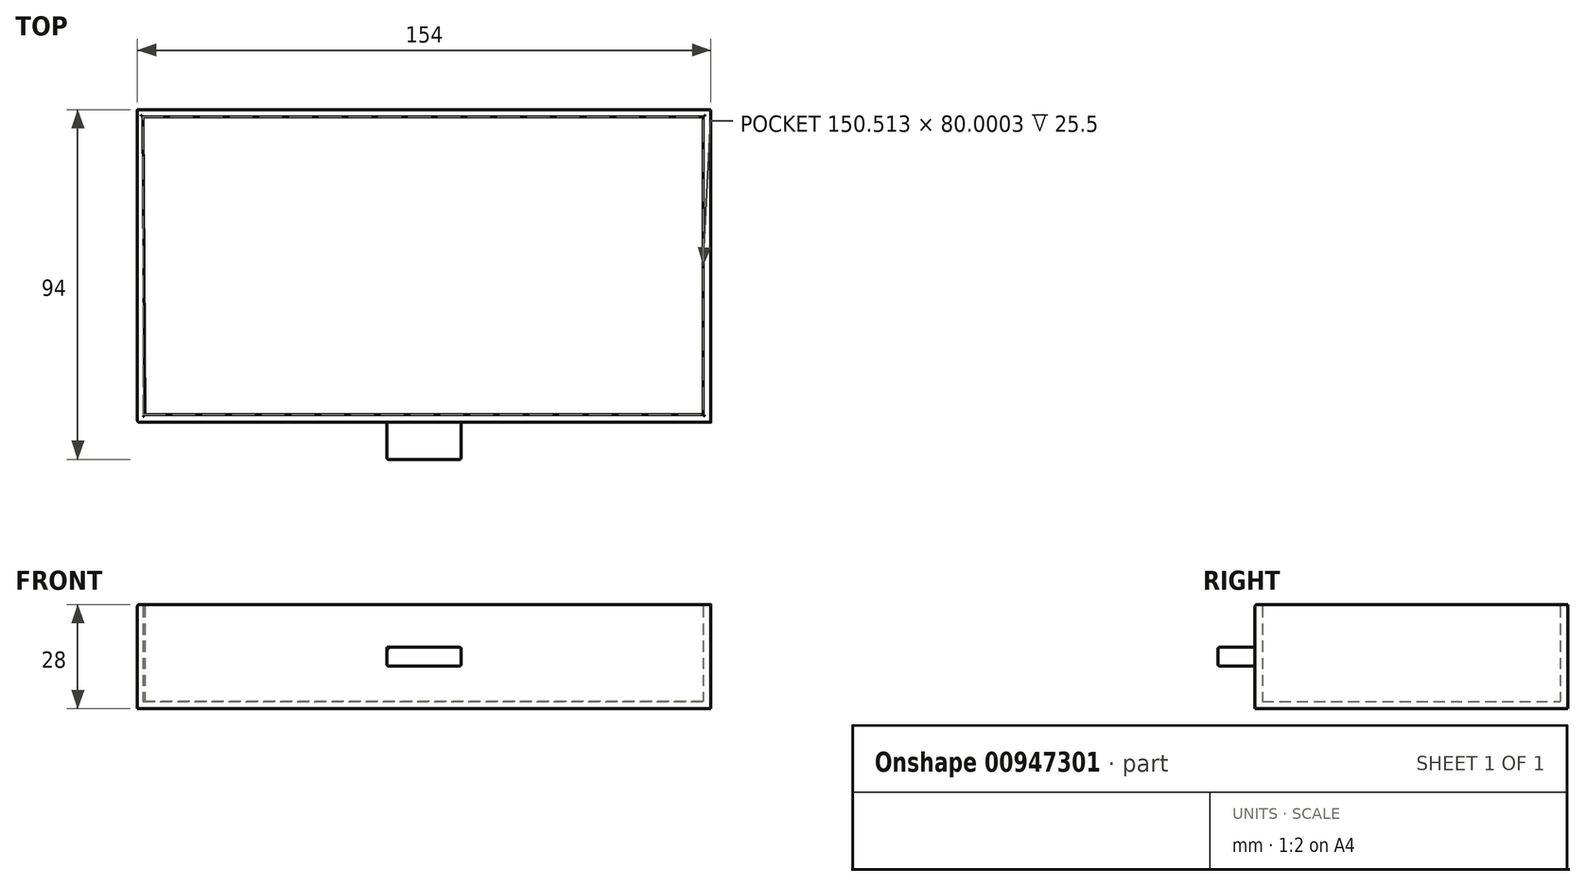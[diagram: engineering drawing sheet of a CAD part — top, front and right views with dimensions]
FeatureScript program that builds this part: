
annotation { "Feature Type Name" : "Feature", "Feature Type Description" : "" }
export const myFeature = defineFeature(function(context is Context, id is Id, definition is map)
    precondition{}
    {
        {
            var Q0;
            Q0=qCreatedBy(makeId("Top.planeOp"),FACE);
            var sketch = newSketch(context, id + "F0", { "sketchPlane" : qUnion([Q0])});
            skLineSegment(sketch, "E0", {"start": v(-84.28, -100) * mm, "end": v(85.72, -100) * mm});
            skLineSegment(sketch, "E1", {"start": v(-84.28, -100) * mm, "end": v(-84.28, 0) * mm});
            skLineSegment(sketch, "E2", {"start": v(85.72, -100) * mm, "end": v(85.72, 0) * mm});
            skLineSegment(sketch, "E3", {"start": v(85.72, 0) * mm, "end": v(-84.28, 0) * mm});
            skSolve(sketch);
        }
        {
            var Q0;
            Q0=makeQuery(id+"F0.imprint","IMPRINT",FACE,{"disambiguationData":[TD([[makeQuery(id+"F0.imprint","IMPRINT",EDGE,{"derivedFrom":sQuery(id+"F0.wireOp",EDGE,"E0")}),1.0]])]});
            extrude(context, id + "F1", {"entities" : qUnion([Q0]), "depth" : 2 * mm, "offsetDistance" : 25 * mm});
        }
        {
            var Q0;
            Q0=makeQuery(id+"F1.opExtrude","CAP_FACE",FACE,{"disambiguationData":[OSD([sQuery(id+"F0.wireOp",EDGE,"E0"),sQuery(id+"F0.wireOp",EDGE,"E1"),sQuery(id+"F0.wireOp",EDGE,"E2"),sQuery(id+"F0.wireOp",EDGE,"E3")])],"isStart":false});
            var sketch = newSketch(context, id + "F2", { "sketchPlane" : qUnion([Q0])});
            skLineSegment(sketch, "E4", {"start": v(83.72, -98) * mm, "end": v(-82.28, -98) * mm});
            skLineSegment(sketch, "E5", {"start": v(83.72, -2) * mm, "end": v(83.72, -98) * mm});
            skLineSegment(sketch, "E6", {"start": v(83.72, -2) * mm, "end": v(-82.9, -2) * mm});
            skLineSegment(sketch, "E7", {"start": v(-82.28, -98) * mm, "end": v(-82.9, -2) * mm});
            skSolve(sketch);
        }
        {
            var Q0;
            Q0=makeQuery(id+"F2.imprint","IMPRINT",FACE,{"disambiguationData":[TD([[makeQuery(id+"F2.imprint","IMPRINT",EDGE,{"derivedFrom":sQuery(id+"F2.wireOp",EDGE,"E4")}),1.0]])]});
            extrude(context, id + "F3", {"entities" : qUnion([Q0]), "operationType" : NewBodyOperationType.ADD, "depth" : 26 * mm, "offsetDistance" : 25 * mm});
        }
        {
            var Q0;
            Q0=makeQuery(id+"F1.opExtrude","CAP_FACE",FACE,{"disambiguationData":[OSD([sQuery(id+"F0.wireOp",EDGE,"E0"),sQuery(id+"F0.wireOp",EDGE,"E1"),sQuery(id+"F0.wireOp",EDGE,"E2"),sQuery(id+"F0.wireOp",EDGE,"E3")])],"isStart":false});
            var sketch = newSketch(context, id + "F4", { "sketchPlane" : qUnion([Q0])});
            skLineSegment(sketch, "E8", {"start": v(83.72, -98) * mm, "end": v(67.72, -98) * mm});
            skLineSegment(sketch, "E9", {"start": v(67.72, -98) * mm, "end": v(67.72, -2) * mm});
            skLineSegment(sketch, "E10", {"start": v(67.72, -2) * mm, "end": v(69.72, -2) * mm});
            skLineSegment(sketch, "E11", {"start": v(69.72, -2) * mm, "end": v(69.72, -98) * mm});
            skLineSegment(sketch, "E12", {"start": v(69.72, -98) * mm, "end": v(67.72, -98) * mm});
            skSolve(sketch);
        }
        {
            var Q0;
            {var subQ0=sQuery(id+"F4.wireOp",EDGE,"E9");Q0=makeQuery(id+"F4.imprint","IMPRINT",FACE,{"disambiguationData":[TD([[makeQuery(id+"F4.imprint","IMPRINT",EDGE,{"derivedFrom":subQ0}),-1.0]])]});}
            extrude(context, id + "F5", {"entities" : qUnion([Q0]), "operationType" : NewBodyOperationType.ADD, "depth" : 26 * mm, "offsetDistance" : 25 * mm});
        }
        {
            var Q0;
            Q0=makeQuery(id+"F5.boolean.opBoolean","MERGE",FACE,{"derivedFrom":[makeQuery(id+"F3.opExtrude","CAP_FACE",FACE,{"disambiguationData":[OSD([sQuery(id+"F0.wireOp",EDGE,"E0"),sQuery(id+"F0.wireOp",EDGE,"E1"),sQuery(id+"F0.wireOp",EDGE,"E2"),sQuery(id+"F0.wireOp",EDGE,"E3"),sQuery(id+"F2.wireOp",EDGE,"E4"),sQuery(id+"F2.wireOp",EDGE,"E5"),sQuery(id+"F2.wireOp",EDGE,"E6"),sQuery(id+"F2.wireOp",EDGE,"E7")])],"isStart":false}),makeQuery(id+"F5.opExtrude","CAP_FACE",FACE,{"disambiguationData":[OSD([sQuery(id+"F4.wireOp",EDGE,"E8"),sQuery(id+"F4.wireOp",EDGE,"E9"),sQuery(id+"F4.wireOp",EDGE,"E10"),sQuery(id+"F4.wireOp",EDGE,"E11")])],"isStart":false})]});
            var sketch = newSketch(context, id + "F6", { "sketchPlane" : qUnion([Q0])});
            skLineSegment(sketch, "E13", {"start": v(69.72, -98) * mm, "end": v(69.72, -100) * mm});
            skLineSegment(sketch, "E14", {"start": v(69.72, -100) * mm, "end": v(85.72, -100) * mm});
            skLineSegment(sketch, "E15", {"start": v(85.72, -100) * mm, "end": v(85.72, 0) * mm});
            skLineSegment(sketch, "E16", {"start": v(85.72, 0) * mm, "end": v(69.72, 0) * mm});
            skLineSegment(sketch, "E17", {"start": v(69.72, 0) * mm, "end": v(69.72, -100) * mm});
            skSolve(sketch);
        }
        {
            var Q0;
            {var subQ4=sQuery(id+"F2.wireOp",EDGE,"E5");Q0=makeQuery(id+"F6.imprint","IMPRINT",FACE,{"disambiguationData":[TD([[makeQuery(id+"F6.imprint","IMPRINT",EDGE,{"derivedFrom":makeQuery(id+"F3.opExtrude","CAP_EDGE",EDGE,{"disambiguationData":[OSD([subQ4])],"isStart":false})}),-1.0]])]});}
            var Q1;
            Q1=makeQuery(id+"F6.imprint","IMPRINT",FACE,{"disambiguationData":[TD([[makeQuery(id+"F6.imprint","IMPRINT",EDGE,{"derivedFrom":sQuery(id+"F6.wireOp",EDGE,"E13")}),1.0]])]});
            extrude(context, id + "F7", {"entities" : qUnion([Q0, Q1]), "operationType" : NewBodyOperationType.REMOVE, "oppositeDirection" : true, "depth" : 30 * mm, "offsetDistance" : 25 * mm});
        }
        {
            var Q0;
            {var subQ0=sQuery(id+"F0.wireOp",EDGE,"E0");Q0=makeQuery(id+"F3.boolean.opBoolean","MERGE",FACE,{"derivedFrom":[makeQuery(id+"F1.opExtrude","SWEPT_FACE",FACE,{"disambiguationData":[OSD([subQ0])]}),makeQuery(id+"F3.opExtrude","SWEPT_FACE",FACE,{"disambiguationData":[OSD([subQ0])]})]});}
            var sketch = newSketch(context, id + "F8", { "sketchPlane" : qUnion([Q0])});
            skLineSegment(sketch, "E18", {"start": v(-84.28, 14) * mm, "end": v(69.72, 14) * mm});
            skLineSegment(sketch, "E19", {"start": v(-7.28, 28) * mm, "end": v(-7.28, 0) * mm});
            skLineSegment(sketch, "E20", {"start": v(-7.28, 14) * mm, "end": v(2.72, 14) * mm});
            skLineSegment(sketch, "E21", {"start": v(2.72, 14) * mm, "end": v(2.72, 16.5) * mm});
            skLineSegment(sketch, "E22", {"start": v(2.72, 16.5) * mm, "end": v(-17.28, 16.5) * mm});
            skLineSegment(sketch, "E23", {"start": v(-17.28, 16.5) * mm, "end": v(-17.28, 11.5) * mm});
            skLineSegment(sketch, "E24", {"start": v(-17.28, 11.5) * mm, "end": v(2.72, 11.5) * mm});
            skLineSegment(sketch, "E25", {"start": v(2.72, 11.5) * mm, "end": v(2.72, 14) * mm});
            skSolve(sketch);
        }
        {
            var Q0;
            {var subQ0=sQuery(id+"F8.wireOp",EDGE,"E21");Q0=makeQuery(id+"F8.imprint","IMPRINT",FACE,{"disambiguationData":[TD([[makeQuery(id+"F8.imprint","IMPRINT",EDGE,{"derivedFrom":subQ0}),1.0]])]});}
            var Q1;
            {var subQ0=sQuery(id+"F8.wireOp",EDGE,"E23");var subQ1=sQuery(id+"F8.wireOp",EDGE,"E18");var subQ2=makeQuery(id+"F8.imprint","INTERSECT",VERTEX,{"derivedFrom":[subQ1,subQ0]});Q1=makeQuery(id+"F8.imprint","IMPRINT",FACE,{"disambiguationData":[TD([[makeQuery(id+"F8.imprint","IMPRINT",EDGE,{"disambiguationData":[TD([[subQ2,-1.0]])],"derivedFrom":subQ1}),1.0]])]});}
            var Q2;
            {var subQ0=sQuery(id+"F8.wireOp",EDGE,"E23");var subQ1=sQuery(id+"F8.wireOp",EDGE,"E18");var subQ2=makeQuery(id+"F8.imprint","INTERSECT",VERTEX,{"derivedFrom":[subQ1,subQ0]});Q2=makeQuery(id+"F8.imprint","IMPRINT",FACE,{"disambiguationData":[TD([[makeQuery(id+"F8.imprint","IMPRINT",EDGE,{"disambiguationData":[TD([[subQ2,-1.0]])],"derivedFrom":subQ1}),-1.0]])]});}
            var Q3;
            {var subQ0=sQuery(id+"F8.wireOp",EDGE,"E25");Q3=makeQuery(id+"F8.imprint","IMPRINT",FACE,{"disambiguationData":[TD([[makeQuery(id+"F8.imprint","IMPRINT",EDGE,{"derivedFrom":subQ0}),1.0]])]});}
            extrude(context, id + "F9", {"entities" : qUnion([Q0, Q1, Q2, Q3]), "operationType" : NewBodyOperationType.ADD, "depth" : 10 * mm, "offsetDistance" : 25 * mm});
        }
        {
            var Q0;
            Q0=makeQuery(id+"F5.boolean.opBoolean","SPLIT",FACE,{"disambiguationData":[TD([makeQuery(id+"F3.opExtrude","SWEPT_FACE",FACE,{"disambiguationData":[OSD([sQuery(id+"F2.wireOp",EDGE,"E7")])]})])],"derivedFrom":makeQuery(id+"F1.opExtrude","CAP_FACE",FACE,{"disambiguationData":[OSD([sQuery(id+"F0.wireOp",EDGE,"E0"),sQuery(id+"F0.wireOp",EDGE,"E1"),sQuery(id+"F0.wireOp",EDGE,"E2"),sQuery(id+"F0.wireOp",EDGE,"E3")])],"isStart":false})});
            var sketch = newSketch(context, id + "F10", { "sketchPlane" : qUnion([Q0])});
            skLineSegment(sketch, "E26", {"start": v(-82.9, -2) * mm, "end": v(-82.8, -18) * mm});
            skLineSegment(sketch, "E27", {"start": v(-82.8, -18) * mm, "end": v(67.72, -18) * mm});
            skLineSegment(sketch, "E28", {"start": v(-82.8, -18) * mm, "end": v(-82.8, -16) * mm});
            skLineSegment(sketch, "E29", {"start": v(-82.8, -16) * mm, "end": v(67.72, -16) * mm});
            skLineSegment(sketch, "E30", {"start": v(67.72, -16) * mm, "end": v(67.72, -18) * mm});
            skSolve(sketch);
        }
        {
            var Q0;
            {var subQ0=sQuery(id+"F10.wireOp",EDGE,"E27");Q0=makeQuery(id+"F10.imprint","IMPRINT",FACE,{"disambiguationData":[TD([[makeQuery(id+"F10.imprint","IMPRINT",EDGE,{"derivedFrom":subQ0}),1.0]])]});}
            extrude(context, id + "F11", {"entities" : qUnion([Q0]), "operationType" : NewBodyOperationType.ADD, "depth" : 26 * mm, "offsetDistance" : 25 * mm});
        }
        {
            var Q0;
            Q0=makeQuery(id+"F11.boolean.opBoolean","MERGE",FACE,{"derivedFrom":[makeQuery(id+"F5.boolean.opBoolean","MERGE",FACE,{"derivedFrom":[makeQuery(id+"F3.opExtrude","CAP_FACE",FACE,{"disambiguationData":[OSD([sQuery(id+"F0.wireOp",EDGE,"E0"),sQuery(id+"F0.wireOp",EDGE,"E1"),sQuery(id+"F0.wireOp",EDGE,"E2"),sQuery(id+"F0.wireOp",EDGE,"E3"),sQuery(id+"F2.wireOp",EDGE,"E4"),sQuery(id+"F2.wireOp",EDGE,"E5"),sQuery(id+"F2.wireOp",EDGE,"E6"),sQuery(id+"F2.wireOp",EDGE,"E7")])],"isStart":false}),makeQuery(id+"F5.opExtrude","CAP_FACE",FACE,{"disambiguationData":[OSD([sQuery(id+"F4.wireOp",EDGE,"E8"),sQuery(id+"F4.wireOp",EDGE,"E9"),sQuery(id+"F4.wireOp",EDGE,"E10"),sQuery(id+"F4.wireOp",EDGE,"E11")])],"isStart":false})]}),makeQuery(id+"F11.opExtrude","CAP_FACE",FACE,{"disambiguationData":[OSD([sQuery(id+"F10.wireOp",EDGE,"E26"),sQuery(id+"F10.wireOp",EDGE,"E27"),sQuery(id+"F10.wireOp",EDGE,"E29"),sQuery(id+"F10.wireOp",EDGE,"E30")])],"isStart":false})]});
            var sketch = newSketch(context, id + "F12", { "sketchPlane" : qUnion([Q0])});
            skLineSegment(sketch, "E31", {"start": v(-82.8, -16) * mm, "end": v(69.72, -16) * mm});
            skLineSegment(sketch, "E32", {"start": v(69.72, -16) * mm, "end": v(69.72, 0) * mm});
            skLineSegment(sketch, "E33", {"start": v(69.72, 0) * mm, "end": v(-84.28, 0) * mm});
            skLineSegment(sketch, "E34", {"start": v(-84.28, 0) * mm, "end": v(-84.28, -16) * mm});
            skLineSegment(sketch, "E35", {"start": v(-84.28, -16) * mm, "end": v(-82.8, -16) * mm});
            skSolve(sketch);
        }
        {
            var Q0;
            {var subQ12=sQuery(id+"F12.wireOp",EDGE,"E32");Q0=makeQuery(id+"F12.imprint","IMPRINT",FACE,{"disambiguationData":[TD([[makeQuery(id+"F12.imprint","IMPRINT",EDGE,{"derivedFrom":subQ12}),-1.0]])]});}
            var Q1;
            {var subQ3=sQuery(id+"F2.wireOp",EDGE,"E7");var subQ4=makeQuery(id+"F3.opExtrude","SWEPT_FACE",FACE,{"disambiguationData":[OSD([subQ3])]});var subQ5=sQuery(id+"F2.wireOp",EDGE,"E6");Q1=makeQuery(id+"F12.imprint","IMPRINT",FACE,{"disambiguationData":[TD([[makeQuery(id+"F12.imprint","IMPRINT",EDGE,{"derivedFrom":makeQuery(id+"F5.boolean.opBoolean","SPLIT",EDGE,{"disambiguationData":[TD([subQ4])],"derivedFrom":makeQuery(id+"F3.opExtrude","CAP_EDGE",EDGE,{"disambiguationData":[OSD([subQ5])],"isStart":false})})}),1.0]])]});}
            extrude(context, id + "F13", {"entities" : qUnion([Q0, Q1]), "operationType" : NewBodyOperationType.REMOVE, "oppositeDirection" : true, "depth" : 30 * mm, "offsetDistance" : 25 * mm});
        }
        {
            var Q0;
            {var subQ0=sQuery(id+"F2.wireOp",EDGE,"E7");var subQ1=sQuery(id+"F2.wireOp",EDGE,"E4");Q0=makeQuery(id+"F11.boolean.opBoolean","SPLIT",EDGE,{"disambiguationData":[TD([makeQuery(id+"F3.opExtrude","SWEPT_FACE",FACE,{"disambiguationData":[OSD([subQ1])]})])],"derivedFrom":makeQuery(id+"F3.opExtrude","CAP_EDGE",EDGE,{"disambiguationData":[OSD([subQ0])],"isStart":false})});}
            var Q1;
            Q1=makeQuery(id+"F11.opExtrude","CAP_EDGE",EDGE,{"disambiguationData":[OSD([sQuery(id+"F10.wireOp",EDGE,"E27")])],"isStart":false});
            var Q2;
            Q2=makeQuery(id+"F13.boolean.opBoolean","MERGE",EDGE,{"derivedFrom":[makeQuery(id+"F11.opExtrude","CAP_EDGE",EDGE,{"disambiguationData":[OSD([sQuery(id+"F10.wireOp",EDGE,"E29")])],"isStart":false})],"fromTools":[makeQuery(id+"F13.opExtrude","CAP_EDGE",EDGE,{"disambiguationData":[OSD([sQuery(id+"F12.wireOp",EDGE,"E31"),sQuery(id+"F12.wireOp",EDGE,"E35")])],"isStart":true})]});
            var Q3;
            Q3=makeQuery(id+"F3.opExtrude","CAP_EDGE",EDGE,{"disambiguationData":[OSD([sQuery(id+"F0.wireOp",EDGE,"E1")])],"isStart":false});
            var Q4;
            {var subQ1=sQuery(id+"F2.wireOp",EDGE,"E7");var subQ2=sQuery(id+"F2.wireOp",EDGE,"E4");Q4=makeQuery(id+"F5.boolean.opBoolean","SPLIT",EDGE,{"disambiguationData":[TD([makeQuery(id+"F3.opExtrude","SWEPT_FACE",FACE,{"disambiguationData":[OSD([subQ1])]})])],"derivedFrom":makeQuery(id+"F3.opExtrude","CAP_EDGE",EDGE,{"disambiguationData":[OSD([subQ2])],"isStart":false})});}
            var Q5;
            Q5=makeQuery(id+"F3.opExtrude","CAP_EDGE",EDGE,{"disambiguationData":[OSD([sQuery(id+"F0.wireOp",EDGE,"E0")])],"isStart":false});
            var Q6;
            {var subQ0=sQuery(id+"F4.wireOp",EDGE,"E9");var subQ1=sQuery(id+"F2.wireOp",EDGE,"E4");Q6=makeQuery(id+"F11.boolean.opBoolean","SPLIT",EDGE,{"disambiguationData":[TD([makeQuery(id+"F3.opExtrude","SWEPT_FACE",FACE,{"disambiguationData":[OSD([subQ1])]})])],"derivedFrom":makeQuery(id+"F5.opExtrude","CAP_EDGE",EDGE,{"disambiguationData":[OSD([subQ0])],"isStart":false})});}
            var Q7;
            Q7=makeQuery(id+"F7.boolean.opBoolean","MERGE",EDGE,{"derivedFrom":[makeQuery(id+"F5.opExtrude","CAP_EDGE",EDGE,{"disambiguationData":[OSD([sQuery(id+"F4.wireOp",EDGE,"E11")])],"isStart":false})],"fromTools":[makeQuery(id+"F7.opExtrude","CAP_EDGE",EDGE,{"disambiguationData":[OSD([sQuery(id+"F6.wireOp",EDGE,"E13"),sQuery(id+"F6.wireOp",EDGE,"E17")])],"isStart":true})]});
            var Q8;
            Q8=makeQuery(id+"F13.boolean.opBoolean","COPY",EDGE,{"derivedFrom":makeQuery(id+"F13.opExtrude","SWEPT_EDGE",EDGE,{"disambiguationData":[OSD([sQuery(id+"F4.wireOp",EDGE,"E11"),sQuery(id+"F6.wireOp",EDGE,"E13"),sQuery(id+"F6.wireOp",EDGE,"E17"),sQuery(id+"F12.wireOp",EDGE,"E31"),sQuery(id+"F12.wireOp",EDGE,"E32")])]})});
            var Q9;
            Q9=makeQuery(id+"F7.boolean.opBoolean","COPY",EDGE,{"derivedFrom":makeQuery(id+"F7.opExtrude","SWEPT_EDGE",EDGE,{"disambiguationData":[OSD([sQuery(id+"F0.wireOp",EDGE,"E0"),sQuery(id+"F6.wireOp",EDGE,"E13"),sQuery(id+"F6.wireOp",EDGE,"E14")])]})});
            var Q10;
            Q10=makeQuery(id+"F9.opExtrude","SWEPT_EDGE",EDGE,{"disambiguationData":[OSD([sQuery(id+"F8.wireOp",EDGE,"E21"),sQuery(id+"F8.wireOp",EDGE,"E22")])]});
            var Q11;
            Q11=makeQuery(id+"F9.opExtrude","SWEPT_EDGE",EDGE,{"disambiguationData":[OSD([sQuery(id+"F8.wireOp",EDGE,"E24"),sQuery(id+"F8.wireOp",EDGE,"E25")])]});
            var Q12;
            Q12=makeQuery(id+"F9.opExtrude","CAP_EDGE",EDGE,{"disambiguationData":[OSD([sQuery(id+"F8.wireOp",EDGE,"E21"),sQuery(id+"F8.wireOp",EDGE,"E25")])],"isStart":true});
            var Q13;
            Q13=makeQuery(id+"F9.opExtrude","CAP_EDGE",EDGE,{"disambiguationData":[OSD([sQuery(id+"F8.wireOp",EDGE,"E22")])],"isStart":true});
            var Q14;
            Q14=makeQuery(id+"F9.opExtrude","CAP_EDGE",EDGE,{"disambiguationData":[OSD([sQuery(id+"F8.wireOp",EDGE,"E22")])],"isStart":false});
            var Q15;
            Q15=makeQuery(id+"F9.opExtrude","CAP_EDGE",EDGE,{"disambiguationData":[OSD([sQuery(id+"F8.wireOp",EDGE,"E24")])],"isStart":false});
            var Q16;
            Q16=makeQuery(id+"F9.opExtrude","CAP_EDGE",EDGE,{"disambiguationData":[OSD([sQuery(id+"F8.wireOp",EDGE,"E23")])],"isStart":false});
            var Q17;
            {var subQ0=sQuery(id+"F0.wireOp",EDGE,"E1");var subQ1=sQuery(id+"F0.wireOp",EDGE,"E0");Q17=makeQuery(id+"F3.boolean.opBoolean","MERGE",EDGE,{"derivedFrom":[makeQuery(id+"F1.opExtrude","SWEPT_EDGE",EDGE,{"disambiguationData":[OSD([subQ1,subQ0])]}),makeQuery(id+"F3.opExtrude","SWEPT_EDGE",EDGE,{"disambiguationData":[OSD([subQ1,subQ0])]})]});}
            var Q18;
            Q18=makeQuery(id+"F13.boolean.opBoolean","COPY",EDGE,{"derivedFrom":makeQuery(id+"F13.opExtrude","SWEPT_EDGE",EDGE,{"disambiguationData":[OSD([sQuery(id+"F0.wireOp",EDGE,"E1"),sQuery(id+"F12.wireOp",EDGE,"E34"),sQuery(id+"F12.wireOp",EDGE,"E35")])]})});
            var Q19;
            Q19=makeQuery(id+"F9.opExtrude","CAP_EDGE",EDGE,{"disambiguationData":[OSD([sQuery(id+"F8.wireOp",EDGE,"E23")])],"isStart":true});
            var Q20;
            Q20=makeQuery(id+"F9.opExtrude","SWEPT_EDGE",EDGE,{"disambiguationData":[OSD([sQuery(id+"F8.wireOp",EDGE,"E23"),sQuery(id+"F8.wireOp",EDGE,"E24")])]});
            var Q21;
            Q21=makeQuery(id+"F9.opExtrude","CAP_EDGE",EDGE,{"disambiguationData":[OSD([sQuery(id+"F8.wireOp",EDGE,"E21"),sQuery(id+"F8.wireOp",EDGE,"E25")])],"isStart":false});
            var Q22;
            Q22=makeQuery(id+"F9.opExtrude","CAP_EDGE",EDGE,{"disambiguationData":[OSD([sQuery(id+"F8.wireOp",EDGE,"E24")])],"isStart":true});
            fillet(context, id + "F14", {"entities" : qUnion([Q0, Q1, Q2, Q3, Q4, Q5, Q6, Q7, Q8, Q9, Q10, Q11, Q12, Q13, Q14, Q15, Q16, Q17, Q18, Q19, Q20, Q21, Q22]), "radius" : 0.5 * mm, "tangentPropagation" : true, "allowEdgeOverflow" : false});
        }
    });
